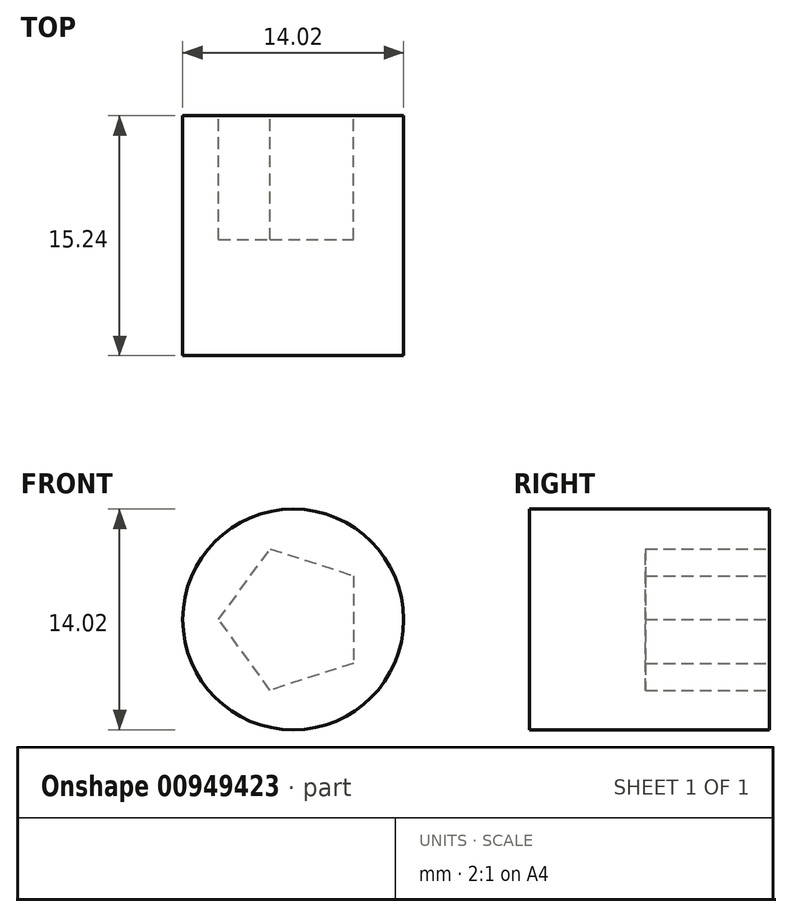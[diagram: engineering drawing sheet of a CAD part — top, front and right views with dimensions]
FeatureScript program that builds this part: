
annotation { "Feature Type Name" : "Feature", "Feature Type Description" : "" }
export const myFeature = defineFeature(function(context is Context, id is Id, definition is map)
    precondition{}
    {
        {
            var Q0;
            Q0=qCreatedBy(makeId("Front.planeOp"),FACE);
            var sketch = newSketch(context, id + "F0", { "sketchPlane" : qUnion([Q0])});
            skCircle(sketch, "E0", {"center": v(0, 0) * mm, "radius": 7.01 * mm});
            skSolve(sketch);
        }
        {
            var Q0;
            Q0=makeQuery(id+"F0.imprint","IMPRINT",FACE,{"disambiguationData":[TD([[makeQuery(id+"F0.imprint","IMPRINT",EDGE,{"derivedFrom":sQuery(id+"F0.wireOp",EDGE,"E0")}),1.0]])]});
            var Q1;
            Q1=sQuery(id+"F0.wireOp",EDGE,"E0");
            extrude(context, id + "F1", {"entities" : qUnion([Q0]), "surfaceEntities" : qUnion([Q1]), "depth" : 15.24 * mm, "offsetDistance" : 25.4 * mm});
        }
        {
            var Q0;
            Q0=qCreatedBy(makeId("Front.planeOp"),FACE);
            var sketch = newSketch(context, id + "F2", { "sketchPlane" : qUnion([Q0])});
            skCircle(sketch, "E1.cCircle", {"center": v(0, 0) * mm, "radius": 3.82 * mm, "construction": true});
            skLineSegment(sketch, "E1.0", {"start": v(3.82, 2.78) * mm, "end": v(3.82, -2.78) * mm});
            skLineSegment(sketch, "E1.1", {"start": v(3.82, -2.78) * mm, "end": v(-1.46, -4.5) * mm});
            skLineSegment(sketch, "E1.2", {"start": v(-1.46, -4.5) * mm, "end": v(-4.72, 0) * mm});
            skLineSegment(sketch, "E1.3", {"start": v(-4.72, 0) * mm, "end": v(-1.46, 4.5) * mm});
            skLineSegment(sketch, "E1.4", {"start": v(-1.46, 4.5) * mm, "end": v(3.82, 2.78) * mm});
            skPoint(sketch, "E1.0.midPoint", {"position": v(3.82, 0) * mm});
            skSolve(sketch);
        }
        {
            var Q0;
            Q0=makeQuery(id+"F2.imprint","IMPRINT",FACE,{"disambiguationData":[TD([[makeQuery(id+"F2.imprint","IMPRINT",EDGE,{"derivedFrom":sQuery(id+"F2.wireOp",EDGE,"E1.0")}),-1.0]])]});
            extrude(context, id + "F3", {"entities" : qUnion([Q0]), "operationType" : NewBodyOperationType.REMOVE, "depth" : 7.87 * mm, "offsetDistance" : 25.4 * mm});
        }
    });
